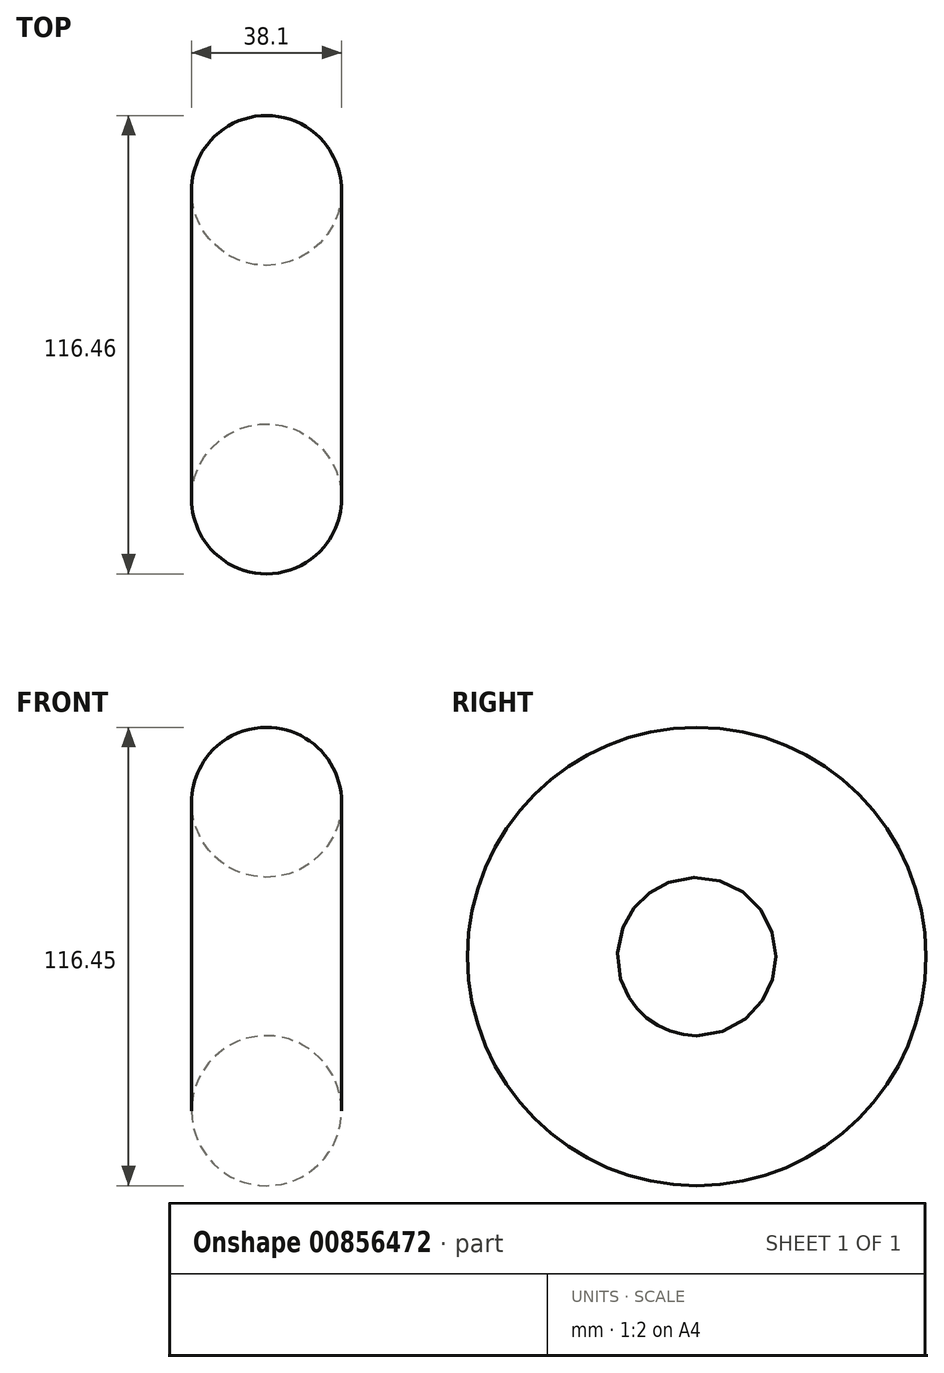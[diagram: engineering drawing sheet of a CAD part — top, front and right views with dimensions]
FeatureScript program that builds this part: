
annotation { "Feature Type Name" : "Feature", "Feature Type Description" : "" }
export const myFeature = defineFeature(function(context is Context, id is Id, definition is map)
    precondition{}
    {
        {
            var Q0;
            Q0=qCreatedBy(makeId("Front.planeOp"),FACE);
            var sketch = newSketch(context, id + "F0", { "sketchPlane" : qUnion([Q0])});
            skCircle(sketch, "E0", {"center": v(0, 0) * mm, "radius": 19.05 * mm});
            skLineSegment(sketch, "E1", {"start": v(76.42, 39.18) * mm, "end": v(-76.42, 39.18) * mm});
            skLineSegment(sketch, "E2", {"start": v(-1199.01, -108.39) * mm, "end": v(1202.74, -43.08) * mm});
            skSolve(sketch);
        }
        {
            var Q0;
            Q0=makeQuery(id+"F0.imprint","IMPRINT",FACE,{"disambiguationData":[TD([[makeQuery(id+"F0.imprint","IMPRINT",EDGE,{"derivedFrom":sQuery(id+"F0.wireOp",EDGE,"E0")}),1.0]])]});
            var Q1;
            Q1=sQuery(id+"F0.wireOp",EDGE,"E1");
            revolve(context, id + "F1", {"surfaceOperationType" : NewSurfaceOperationType.NEW, "entities" : qUnion([Q0]), "axis" : qUnion([Q1]), "revolveType" : RevolveType.FULL});
        }
    });
